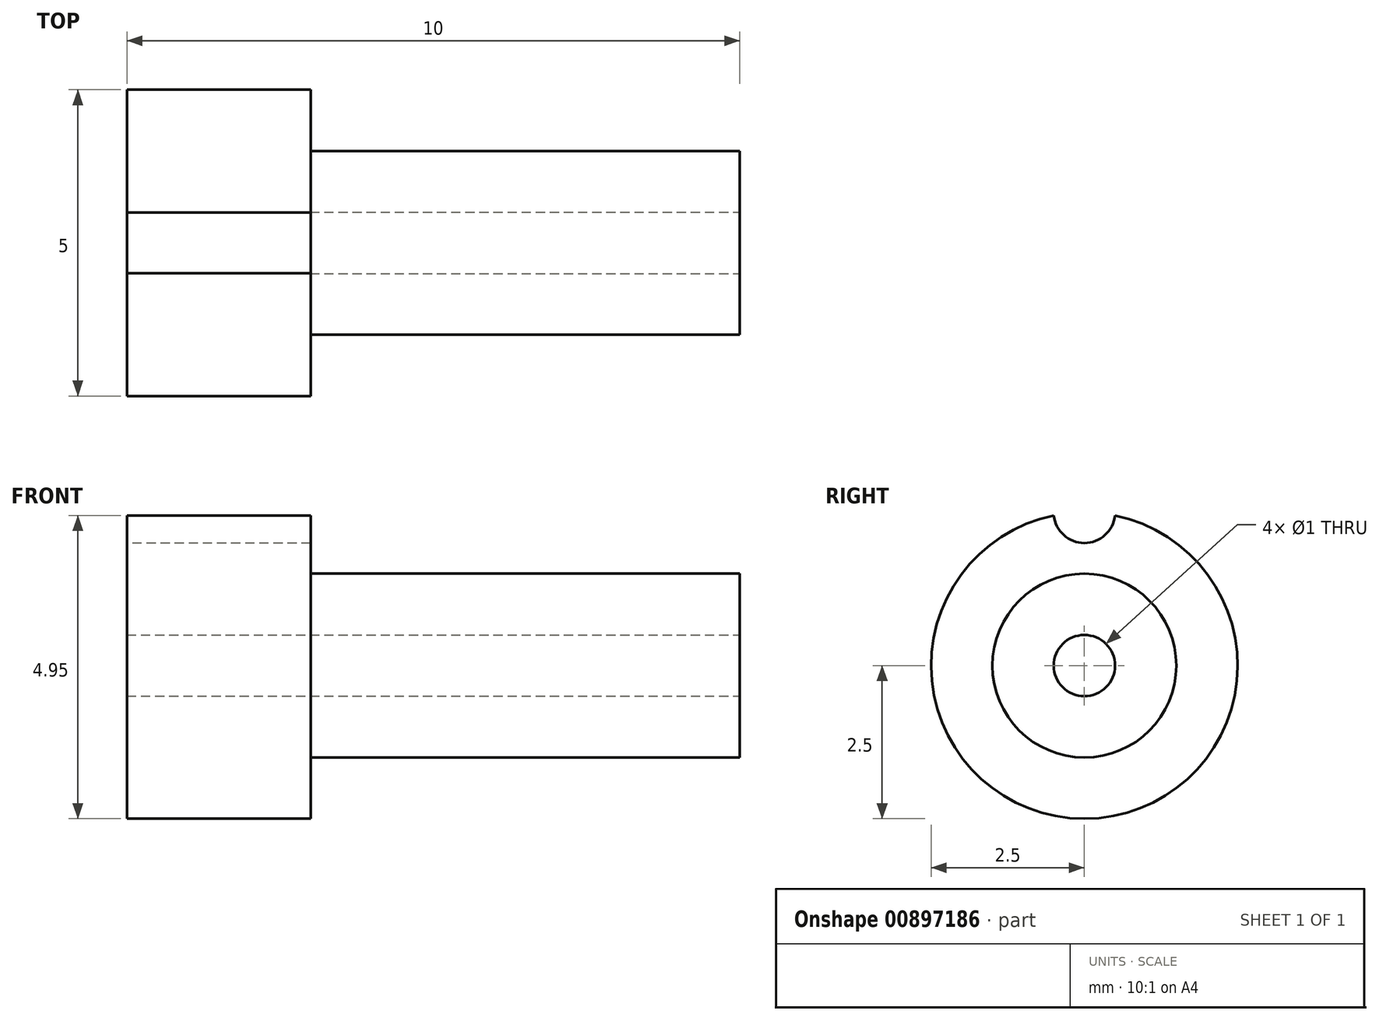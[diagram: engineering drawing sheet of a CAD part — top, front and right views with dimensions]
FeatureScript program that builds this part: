
annotation { "Feature Type Name" : "Feature", "Feature Type Description" : "" }
export const myFeature = defineFeature(function(context is Context, id is Id, definition is map)
    precondition{}
    {
        {
            var Q0;
            Q0=qCreatedBy(makeId("Top.planeOp"),FACE);
            var sketch = newSketch(context, id + "F0", { "sketchPlane" : qUnion([Q0])});
            skLineSegment(sketch, "E0.bottom", {"start": v(0, 0) * mm, "end": v(10, 0) * mm});
            skLineSegment(sketch, "E0.top", {"start": v(3, 1.5) * mm, "end": v(10, 1.5) * mm});
            skLineSegment(sketch, "E0.left", {"start": v(0, 0) * mm, "end": v(0, 1.5) * mm});
            skLineSegment(sketch, "E0.right", {"start": v(10, 0) * mm, "end": v(10, 1.5) * mm});
            skLineSegment(sketch, "E1.bottom", {"start": v(0, 0) * mm, "end": v(3, 0) * mm});
            skLineSegment(sketch, "E1.top", {"start": v(0, 2.5) * mm, "end": v(3, 2.5) * mm});
            skLineSegment(sketch, "E1.left", {"start": v(0, 0) * mm, "end": v(0, 2.5) * mm});
            skLineSegment(sketch, "E1.right", {"start": v(3, 0) * mm, "end": v(3, 2.5) * mm});
            skSolve(sketch);
        }
        {
            var Q0;
            Q0 = qSketchRegion(id + "F0", true);
            var Q1;
            Q1=sQuery(id+"F0.wireOp",EDGE,"E0.bottom");
            revolve(context, id + "F1", {"surfaceOperationType" : NewSurfaceOperationType.NEW, "entities" : qUnion([Q0]), "axis" : qUnion([Q1]), "revolveType" : RevolveType.FULL});
        }
        {
            var Q0;
            Q0=makeQuery(id+"F1.opRevolve","SWEPT_FACE",FACE,{"disambiguationData":[OSD([sQuery(id+"F0.wireOp",EDGE,"E0.right")])]});
            var sketch = newSketch(context, id + "F2", { "sketchPlane" : qUnion([Q0])});
            skCircle(sketch, "E2", {"center": v(0, 0) * mm, "radius": 0.5 * mm});
            skSolve(sketch);
        }
        {
            var Q0;
            Q0=makeQuery(id+"F2.imprint","IMPRINT",FACE,{"disambiguationData":[TD([[makeQuery(id+"F2.imprint","IMPRINT",EDGE,{"derivedFrom":sQuery(id+"F2.wireOp",EDGE,"E2")}),1.0]])]});
            extrude(context, id + "F3", {"entities" : qUnion([Q0]), "operationType" : NewBodyOperationType.REMOVE, "oppositeDirection" : true, "depth" : 10 * mm, "offsetDistance" : 25 * mm});
        }
        {
            var Q0;
            Q0=makeQuery(id+"F1.opRevolve","SWEPT_FACE",FACE,{"disambiguationData":[OSD([sQuery(id+"F0.wireOp",EDGE,"E1.left")])]});
            var sketch = newSketch(context, id + "F4", { "sketchPlane" : qUnion([Q0])});
            skCircle(sketch, "E3", {"center": v(0, 2.5) * mm, "radius": 0.5 * mm});
            skSolve(sketch);
        }
        {
            var Q0;
            {var subQ0=sQuery(id+"F4.wireOp",EDGE,"E3");var subQ1=makeQuery(id+"F1.opRevolve","SWEPT_EDGE",EDGE,{"disambiguationData":[OSD([sQuery(id+"F0.wireOp",EDGE,"E1.top"),sQuery(id+"F0.wireOp",EDGE,"E1.left")])]});var subQ2=makeQuery(id+"F4.imprint","INTERSECT",VERTEX,{"disambiguationData":[OD(0.0)],"derivedFrom":[subQ1,subQ0]});Q0=makeQuery(id+"F4.imprint","IMPRINT",FACE,{"disambiguationData":[TD([[makeQuery(id+"F4.imprint","IMPRINT",EDGE,{"disambiguationData":[TD([[subQ2,1.0]])],"derivedFrom":subQ0}),1.0]])]});}
            extrude(context, id + "F5", {"entities" : qUnion([Q0]), "operationType" : NewBodyOperationType.REMOVE, "oppositeDirection" : true, "depth" : 3 * mm, "offsetDistance" : 25 * mm});
        }
    });
